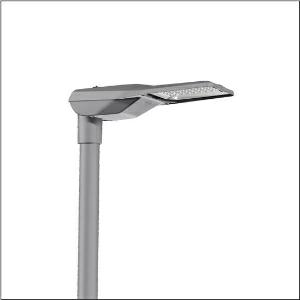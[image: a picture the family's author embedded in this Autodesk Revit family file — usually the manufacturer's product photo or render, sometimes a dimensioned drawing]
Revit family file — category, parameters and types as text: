
# Revit family: streetlight_sl_21_mini___st1_0ab_5xe2m33s08gb_a984
name_source: partatom
category: Lighting Fixtures
units: mm (PartAtom-declared; Revit-internal decimal feet)

## family parameters
Cut with Voids When Loaded = No
Host = Face
Light Source = No
Part Type = Normal
Room Calculation Point = No
Round Connector Dimension = Use Diameter
Shared = No

## types (1)
- --- (1 x LED, 5230 lm, 40.4 W, 3000K)
    Apparent Load = 40 VA
    CIE Flux Codes = 38 73 97 100 100
    Color Rendering = 70
    Color Temperature = 3000K
    Default Elevation = 1800 mm
    Description = Streetlight SL 21 mini, mast luminaire, primary light control with lens, of PMMA, primary optical cover: cover, of toughened safety glass, transparent, light distribution: ST1.0aB, light emission: direct distribution, primary light characteristic: asymmetric, installation type: side-entry, post-top, LED, High Power LED, rated luminous flux: 5.230lm, luminous efficacy: 130lm/W, light colour: 730, colour temperature: 3000K, control gear: D4i, control: flexible luminous flux parameterisation, time-dependent luminous flux control, constant luminous flux control, overheat protection, pre-setting: logarithmic dimming characteristic, mains connection: 220..240V, AC, 50/60Hz, start of lifetime: 40W, end of service life: 41W, reduction: 19W, luminaire housing, of diecast aluminium, powder-coated, Siteco® metallic grey (DB 702S), corrosivity category C5 high according to DIN EN ISO 12944, please order mast flange separately, inclination adjustable: 0°, 5°, 10°, 15°, sealing non-destructively replaceable, multi-level sealing system, length: 628mm, width: 235mm, height: 110mm, mast flange for spigot size: 42mm (side-entry): 5XC10008XM4, 60/48mm (side-entry/post-top): 5XC10108XM2, 76/60mm (side-entry/post-top): 5XC10108XM1, mounting height: 4..8m, Smart Interface above, protection rating (complete): IP66, insulation class (complete): insulation class II (safety insulation), certification: CE, ENEC, ENEC+, VDE, impact resistance: IK10, permissible operating ambient temperature for outdoor applications: -40..+50°C, standard-compliant lighting for roads and squares, packaging unit: 1 piece

Light Distribution: ST1.0aB
    Height = 110 mm
    Lamp = 1 x LED
    Lamp Light Flux = 5230 lm
    Lamp Power = 40.4 W
    Lamp count = 1
    Length = 625 mm
    Luminous efficacy = 129 lm/W
    Manufacturer = Siteco
    ModVariant = No
    Model = 5XE2M33S08GB
    Number of Poles = 1
    OnlyDefault = Yes
    Power Factor = 1
    Product Name = Streetlight SL 21 mini | ST1.0aB
    Product group = mast luminaire | pylon top
    ProductGroupID = 6100
    Protection Class = Protection class II
    Protection Degree = IP 66
    RLX_Detail_Level = 1
    RLX_Emergency_Light_Flux = 0 lm
    RLX_Emergency_Type = 0
    RLX_Emergency_Type_DB = No
    RlxData = <blob elided: 26221 chars, md5=c66e1b5d>
    Socket = socket
    Standby Power = 0 W
    System Light Flux = 5230 lm
    System Power = 40 W
    Type Comments = factory setting: luminous flux: 100 % | dim-lin: 254 | 812 mA
    Type Image = l_1003515.jpg
    URL = http://relux.com
    VarID = @adj_183863
    Voltage = 0 V
    Weight = 0.00 kg
    Width = 234 mm

## geometry (parser evidence)
native form markers: Blend x4, Sweep x13
no freeform markers — native parametric forms only
